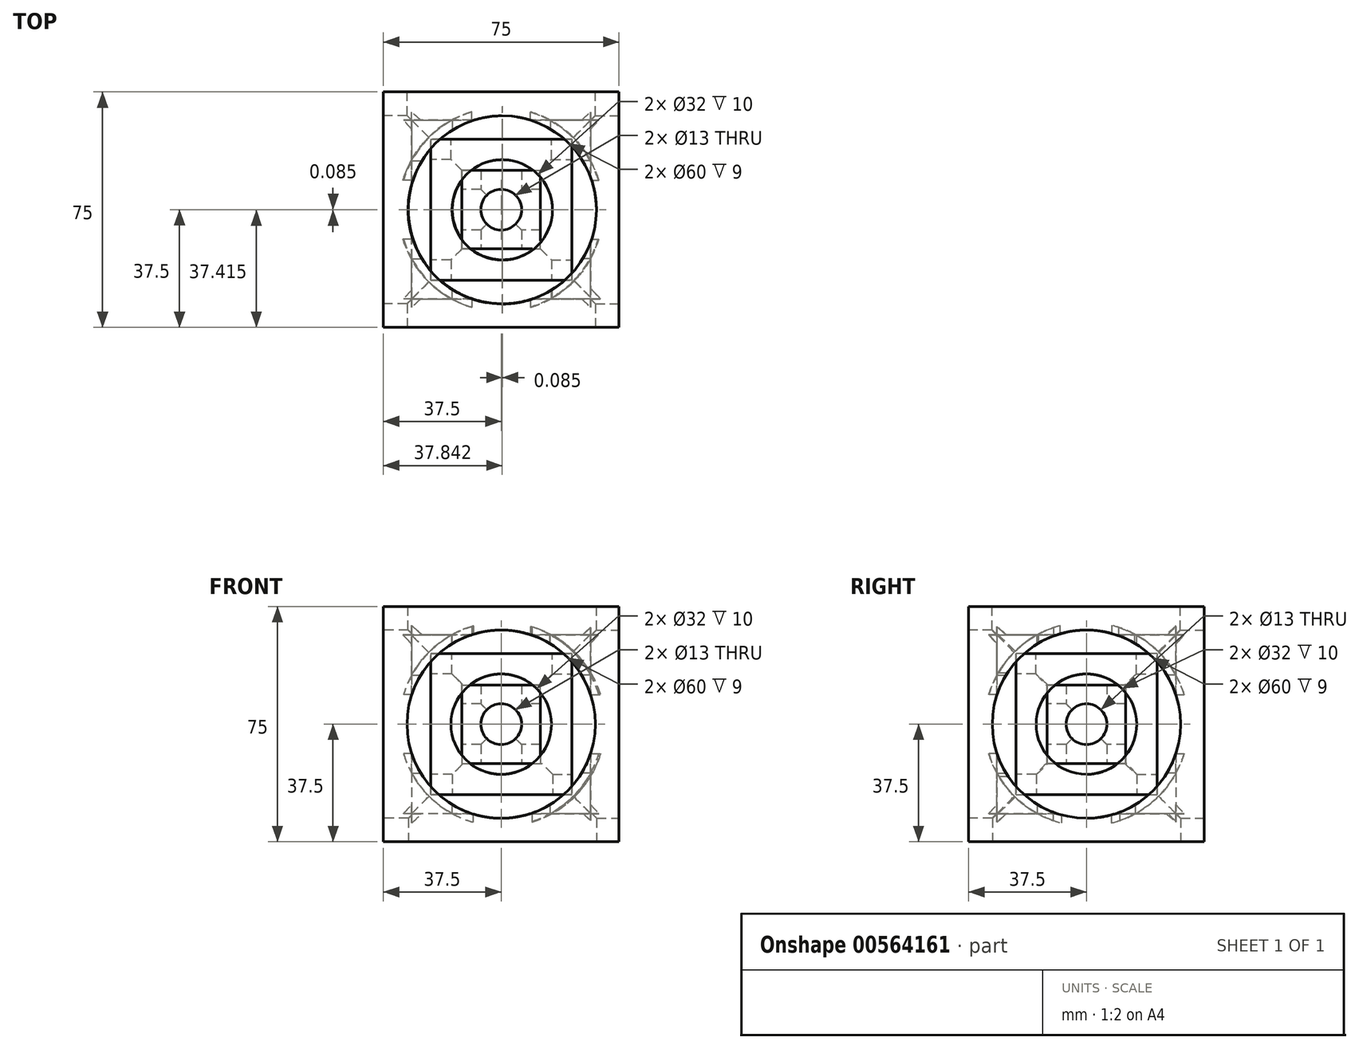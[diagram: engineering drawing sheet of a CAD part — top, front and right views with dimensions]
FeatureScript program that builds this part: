
annotation { "Feature Type Name" : "Feature", "Feature Type Description" : "" }
export const myFeature = defineFeature(function(context is Context, id is Id, definition is map)
    precondition{}
    {
        {
            assignVariable(context, id + "F0", {"name" : "S0", "anyValue" : 75});
        }
        {
            assignVariable(context, id + "F1", {"name" : "D1", "anyValue" : 15});
        }
        {
            assignVariable(context, id + "F2", {"name" : "D2", "anyValue" : 10});
        }
        {
            assignVariable(context, id + "F3", {"name" : "UcutW", "anyValue" : 6});
        }
        {
            var Q0;
            Q0=qCreatedBy(makeId("Front.planeOp"),FACE);
            var sketch = newSketch(context, id + "F4", { "sketchPlane" : qUnion([Q0])});
            skLineSegment(sketch, "E0", {"start": v(0, 0) * mm, "end": v(37.5, 0) * mm, "construction": true});
            skLineSegment(sketch, "E1", {"start": v(37.5, 0) * mm, "end": v(37.5, 37.5) * mm});
            skLineSegment(sketch, "E2", {"start": v(37.5, 37.5) * mm, "end": v(-37.5, 37.5) * mm});
            skLineSegment(sketch, "E3", {"start": v(-37.5, 37.5) * mm, "end": v(-37.5, -37.5) * mm});
            skLineSegment(sketch, "E4", {"start": v(-37.5, -37.5) * mm, "end": v(37.5, -37.5) * mm});
            skLineSegment(sketch, "E5", {"start": v(37.5, -37.5) * mm, "end": v(37.5, 0) * mm});
            skSolve(sketch);
        }
        {
            var Q0;
            Q0 = qSketchRegion(id + "F4", true);
            extrude(context, id + "F5", {"entities" : qUnion([Q0]), "depth" : (getVariable(context, 'S0')) * mm, "offsetDistance" : 25 * mm, "symmetric" : true});
        }
        {
            var Q0;
            Q0=makeQuery(id+"F5.opExtrude","CAP_FACE",FACE,{"disambiguationData":[OSD([sQuery(id+"F4.wireOp",EDGE,"E1"),sQuery(id+"F4.wireOp",EDGE,"E2"),sQuery(id+"F4.wireOp",EDGE,"E3"),sQuery(id+"F4.wireOp",EDGE,"E4"),sQuery(id+"F4.wireOp",EDGE,"E5")])],"isStart":true});
            var sketch = newSketch(context, id + "F6", { "sketchPlane" : qUnion([Q0])});
            skCircle(sketch, "E6", {"center": v(0, 0) * mm, "radius": 30 * mm});
            skCircle(sketch, "E7", {"center": v(0, 0) * mm, "radius": 16 * mm});
            skText(sketch, "E8", { "text": "Ref face", "fontName": "OpenSans-Regular.ttf"});
            const initialGuessF6  = {"E8": [0.0082, -0.03528, 1, 0, 0.0053]};
            skSetInitialGuess(sketch, initialGuessF6);
            skSolve(sketch);
        }
        {
            var Q0;
            Q0=makeQuery(id+"F6.imprint","IMPRINT",FACE,{"disambiguationData":[TD([[makeQuery(id+"F6.imprint","IMPRINT",EDGE,{"derivedFrom":sQuery(id+"F6.wireOp",EDGE,"E6")}),1.0]])]});
            extrude(context, id + "F7", {"entities" : qUnion([Q0]), "operationType" : NewBodyOperationType.REMOVE, "oppositeDirection" : true, "depth" : (getVariable(context, 'D1')) * mm, "offsetDistance" : 25 * mm});
        }
        {
            var Q0;
            Q0=makeQuery(id+"F7.boolean.opBoolean","SPLIT",FACE,{"disambiguationData":[TD([makeQuery(id+"F7.opExtrude","SWEPT_FACE",FACE,{"disambiguationData":[OSD([sQuery(id+"F6.wireOp",EDGE,"E7")])]})])],"derivedFrom":makeQuery(id+"F5.opExtrude","CAP_FACE",FACE,{"disambiguationData":[OSD([sQuery(id+"F4.wireOp",EDGE,"E1"),sQuery(id+"F4.wireOp",EDGE,"E2"),sQuery(id+"F4.wireOp",EDGE,"E3"),sQuery(id+"F4.wireOp",EDGE,"E4"),sQuery(id+"F4.wireOp",EDGE,"E5")])],"isStart":true})});
            extrude(context, id + "F8", {"entities" : qUnion([Q0]), "operationType" : NewBodyOperationType.REMOVE, "oppositeDirection" : true, "depth" : (getVariable(context, 'D1') + getVariable(context, 'D2')) * mm, "offsetDistance" : 25 * mm});
        }
        {
            var Q0;
            Q0=makeQuery(id+"F5.opExtrude","SWEPT_FACE",FACE,{"disambiguationData":[OSD([sQuery(id+"F4.wireOp",EDGE,"E3")])]});
            var sketch = newSketch(context, id + "F9", { "sketchPlane" : qUnion([Q0])});
            skCircle(sketch, "E9", {"center": v(0, 0) * mm, "radius": 30 * mm});
            skCircle(sketch, "E10", {"center": v(0, 0) * mm, "radius": 16 * mm});
            skSolve(sketch);
        }
        {
            var Q0;
            Q0=makeQuery(id+"F9.imprint","IMPRINT",FACE,{"disambiguationData":[TD([[makeQuery(id+"F9.imprint","IMPRINT",EDGE,{"derivedFrom":sQuery(id+"F9.wireOp",EDGE,"E9")}),1.0]])]});
            extrude(context, id + "F10", {"entities" : qUnion([Q0]), "operationType" : NewBodyOperationType.REMOVE, "oppositeDirection" : true, "depth" : (getVariable(context, 'D1')) * mm, "offsetDistance" : 25 * mm});
        }
        {
            var Q0;
            Q0=makeQuery(id+"F10.boolean.opBoolean","SPLIT",FACE,{"disambiguationData":[TD([makeQuery(id+"F10.opExtrude","SWEPT_FACE",FACE,{"disambiguationData":[OSD([sQuery(id+"F9.wireOp",EDGE,"E10")])]})])],"derivedFrom":makeQuery(id+"F5.opExtrude","SWEPT_FACE",FACE,{"disambiguationData":[OSD([sQuery(id+"F4.wireOp",EDGE,"E3")])]})});
            extrude(context, id + "F11", {"entities" : qUnion([Q0]), "operationType" : NewBodyOperationType.REMOVE, "oppositeDirection" : true, "depth" : (getVariable(context, 'D1') + getVariable(context, 'D2')) * mm, "offsetDistance" : 25 * mm});
        }
        {
            var Q0;
            Q0=makeQuery(id+"F5.opExtrude","CAP_FACE",FACE,{"disambiguationData":[OSD([sQuery(id+"F4.wireOp",EDGE,"E1"),sQuery(id+"F4.wireOp",EDGE,"E2"),sQuery(id+"F4.wireOp",EDGE,"E3"),sQuery(id+"F4.wireOp",EDGE,"E4"),sQuery(id+"F4.wireOp",EDGE,"E5")])],"isStart":false});
            var sketch = newSketch(context, id + "F12", { "sketchPlane" : qUnion([Q0])});
            skCircle(sketch, "E11", {"center": v(0, 0) * mm, "radius": 30 * mm});
            skCircle(sketch, "E12", {"center": v(0, 0) * mm, "radius": 16 * mm});
            skSolve(sketch);
        }
        {
            var Q0;
            Q0=makeQuery(id+"F12.imprint","IMPRINT",FACE,{"disambiguationData":[TD([[makeQuery(id+"F12.imprint","IMPRINT",EDGE,{"derivedFrom":sQuery(id+"F12.wireOp",EDGE,"E11")}),1.0]])]});
            extrude(context, id + "F13", {"entities" : qUnion([Q0]), "operationType" : NewBodyOperationType.REMOVE, "oppositeDirection" : true, "depth" : (getVariable(context, 'D1')) * mm, "offsetDistance" : 25 * mm});
        }
        {
            var Q0;
            Q0=makeQuery(id+"F13.boolean.opBoolean","SPLIT",FACE,{"disambiguationData":[TD([makeQuery(id+"F13.opExtrude","SWEPT_FACE",FACE,{"disambiguationData":[OSD([sQuery(id+"F12.wireOp",EDGE,"E12")])]})])],"derivedFrom":makeQuery(id+"F5.opExtrude","CAP_FACE",FACE,{"disambiguationData":[OSD([sQuery(id+"F4.wireOp",EDGE,"E1"),sQuery(id+"F4.wireOp",EDGE,"E2"),sQuery(id+"F4.wireOp",EDGE,"E3"),sQuery(id+"F4.wireOp",EDGE,"E4"),sQuery(id+"F4.wireOp",EDGE,"E5")])],"isStart":false})});
            extrude(context, id + "F14", {"entities" : qUnion([Q0]), "operationType" : NewBodyOperationType.REMOVE, "oppositeDirection" : true, "depth" : (getVariable(context, 'D1') + getVariable(context, 'D2')) * mm, "offsetDistance" : 25 * mm});
        }
        {
            var Q0;
            Q0=makeQuery(id+"F5.opExtrude","SWEPT_FACE",FACE,{"disambiguationData":[OSD([sQuery(id+"F4.wireOp",EDGE,"E1"),sQuery(id+"F4.wireOp",EDGE,"E5")])]});
            var sketch = newSketch(context, id + "F15", { "sketchPlane" : qUnion([Q0])});
            skCircle(sketch, "E13", {"center": v(0, 0) * mm, "radius": 30 * mm});
            skCircle(sketch, "E14", {"center": v(0, 0) * mm, "radius": 16 * mm});
            skSolve(sketch);
        }
        {
            var Q0;
            Q0=makeQuery(id+"F15.imprint","IMPRINT",FACE,{"disambiguationData":[TD([[makeQuery(id+"F15.imprint","IMPRINT",EDGE,{"derivedFrom":sQuery(id+"F15.wireOp",EDGE,"E13")}),1.0]])]});
            extrude(context, id + "F16", {"entities" : qUnion([Q0]), "operationType" : NewBodyOperationType.REMOVE, "oppositeDirection" : true, "depth" : (getVariable(context, 'D1')) * mm, "offsetDistance" : 25 * mm});
        }
        {
            var Q0;
            Q0=makeQuery(id+"F16.boolean.opBoolean","SPLIT",FACE,{"disambiguationData":[TD([makeQuery(id+"F16.opExtrude","SWEPT_FACE",FACE,{"disambiguationData":[OSD([sQuery(id+"F15.wireOp",EDGE,"E14")])]})])],"derivedFrom":makeQuery(id+"F5.opExtrude","SWEPT_FACE",FACE,{"disambiguationData":[OSD([sQuery(id+"F4.wireOp",EDGE,"E1"),sQuery(id+"F4.wireOp",EDGE,"E5")])]})});
            extrude(context, id + "F17", {"entities" : qUnion([Q0]), "operationType" : NewBodyOperationType.REMOVE, "oppositeDirection" : true, "depth" : (getVariable(context, 'D1') + getVariable(context, 'D2')) * mm, "offsetDistance" : 25 * mm});
        }
        {
            var Q0;
            Q0=makeQuery(id+"F5.opExtrude","SWEPT_FACE",FACE,{"disambiguationData":[OSD([sQuery(id+"F4.wireOp",EDGE,"E2")])]});
            var sketch = newSketch(context, id + "F18", { "sketchPlane" : qUnion([Q0])});
            skCircle(sketch, "E15", {"center": v(0.34, -0.09) * mm, "radius": 30 * mm});
            skCircle(sketch, "E16", {"center": v(0.34, -0.09) * mm, "radius": 16 * mm});
            skSolve(sketch);
        }
        {
            var Q0;
            Q0=makeQuery(id+"F18.imprint","IMPRINT",FACE,{"disambiguationData":[TD([[makeQuery(id+"F18.imprint","IMPRINT",EDGE,{"derivedFrom":sQuery(id+"F18.wireOp",EDGE,"E15")}),1.0]])]});
            extrude(context, id + "F19", {"entities" : qUnion([Q0]), "operationType" : NewBodyOperationType.REMOVE, "oppositeDirection" : true, "depth" : (getVariable(context, 'D1')) * mm, "offsetDistance" : 25 * mm});
        }
        {
            var Q0;
            Q0=makeQuery(id+"F19.boolean.opBoolean","SPLIT",FACE,{"disambiguationData":[TD([makeQuery(id+"F19.opExtrude","SWEPT_FACE",FACE,{"disambiguationData":[OSD([sQuery(id+"F18.wireOp",EDGE,"E16")])]})])],"derivedFrom":makeQuery(id+"F5.opExtrude","SWEPT_FACE",FACE,{"disambiguationData":[OSD([sQuery(id+"F4.wireOp",EDGE,"E2")])]})});
            extrude(context, id + "F20", {"entities" : qUnion([Q0]), "operationType" : NewBodyOperationType.REMOVE, "oppositeDirection" : true, "depth" : (getVariable(context, 'D1') + getVariable(context, 'D2')) * mm, "offsetDistance" : 25 * mm});
        }
        {
            var Q0;
            Q0=makeQuery(id+"F5.opExtrude","SWEPT_FACE",FACE,{"disambiguationData":[OSD([sQuery(id+"F4.wireOp",EDGE,"E4")])]});
            var sketch = newSketch(context, id + "F21", { "sketchPlane" : qUnion([Q0])});
            skCircle(sketch, "E17", {"center": v(0.43, 0) * mm, "radius": 30 * mm});
            skCircle(sketch, "E18", {"center": v(0.43, 0) * mm, "radius": 16 * mm});
            skSolve(sketch);
        }
        {
            var Q0;
            Q0=makeQuery(id+"F21.imprint","IMPRINT",FACE,{"disambiguationData":[TD([[makeQuery(id+"F21.imprint","IMPRINT",EDGE,{"derivedFrom":sQuery(id+"F21.wireOp",EDGE,"E17")}),1.0]])]});
            extrude(context, id + "F22", {"entities" : qUnion([Q0]), "operationType" : NewBodyOperationType.REMOVE, "oppositeDirection" : true, "depth" : (getVariable(context, 'D1')) * mm, "offsetDistance" : 25 * mm});
        }
        {
            var Q0;
            Q0=makeQuery(id+"F22.boolean.opBoolean","SPLIT",FACE,{"disambiguationData":[TD([makeQuery(id+"F22.opExtrude","SWEPT_FACE",FACE,{"disambiguationData":[OSD([sQuery(id+"F21.wireOp",EDGE,"E18")])]})])],"derivedFrom":makeQuery(id+"F5.opExtrude","SWEPT_FACE",FACE,{"disambiguationData":[OSD([sQuery(id+"F4.wireOp",EDGE,"E4")])]})});
            extrude(context, id + "F23", {"entities" : qUnion([Q0]), "operationType" : NewBodyOperationType.REMOVE, "oppositeDirection" : true, "depth" : (getVariable(context, 'D1') + getVariable(context, 'D2')) * mm, "offsetDistance" : 25 * mm});
        }
        {
            var Q0;
            Q0=makeQuery(id+"F11.boolean.opBoolean","COPY",FACE,{"derivedFrom":makeQuery(id+"F11.opExtrude","CAP_FACE",FACE,{"disambiguationData":[OSD([sQuery(id+"F4.wireOp",EDGE,"E3")])],"isStart":false})});
            var sketch = newSketch(context, id + "F24", { "sketchPlane" : qUnion([Q0])});
            skCircle(sketch, "E19", {"center": v(0, 0) * mm, "radius": 6.5 * mm});
            skSolve(sketch);
        }
        {
            var Q0;
            Q0 = qSketchRegion(id + "F24", true);
            extrude(context, id + "F25", {"entities" : qUnion([Q0]), "operationType" : NewBodyOperationType.REMOVE, "endBound" : BoundingType.THROUGH_ALL, "oppositeDirection" : true, "depth" : 25 * mm, "offsetDistance" : 25 * mm});
        }
        {
            var Q0;
            Q0=makeQuery(id+"F14.boolean.opBoolean","COPY",FACE,{"derivedFrom":makeQuery(id+"F14.opExtrude","CAP_FACE",FACE,{"disambiguationData":[OSD([sQuery(id+"F4.wireOp",EDGE,"E1"),sQuery(id+"F4.wireOp",EDGE,"E2"),sQuery(id+"F4.wireOp",EDGE,"E3"),sQuery(id+"F4.wireOp",EDGE,"E4"),sQuery(id+"F4.wireOp",EDGE,"E5")])],"isStart":false})});
            var sketch = newSketch(context, id + "F26", { "sketchPlane" : qUnion([Q0])});
            skCircle(sketch, "E20", {"center": v(0, 0) * mm, "radius": 6.5 * mm});
            skSolve(sketch);
        }
        {
            var Q0;
            Q0 = qSketchRegion(id + "F26", true);
            extrude(context, id + "F27", {"entities" : qUnion([Q0]), "operationType" : NewBodyOperationType.REMOVE, "endBound" : BoundingType.THROUGH_ALL, "oppositeDirection" : true, "depth" : 25 * mm, "offsetDistance" : 25 * mm});
        }
        {
            var Q0;
            Q0=makeQuery(id+"F23.boolean.opBoolean","COPY",FACE,{"derivedFrom":makeQuery(id+"F23.opExtrude","CAP_FACE",FACE,{"disambiguationData":[OSD([sQuery(id+"F4.wireOp",EDGE,"E4")])],"isStart":false})});
            var sketch = newSketch(context, id + "F28", { "sketchPlane" : qUnion([Q0])});
            skCircle(sketch, "E21", {"center": v(0, 0) * mm, "radius": 6.5 * mm});
            skSolve(sketch);
        }
        {
            var Q0;
            Q0 = qSketchRegion(id + "F28", true);
            extrude(context, id + "F29", {"entities" : qUnion([Q0]), "operationType" : NewBodyOperationType.REMOVE, "endBound" : BoundingType.THROUGH_ALL, "oppositeDirection" : true, "depth" : 25 * mm, "offsetDistance" : 25 * mm});
        }
        {
            var Q0;
            Q0=makeQuery(id+"F13.boolean.opBoolean","COPY",FACE,{"derivedFrom":makeQuery(id+"F13.opExtrude","CAP_FACE",FACE,{"disambiguationData":[OSD([sQuery(id+"F12.wireOp",EDGE,"E11"),sQuery(id+"F12.wireOp",EDGE,"E12")])],"isStart":false})});
            var sketch = newSketch(context, id + "F30", { "sketchPlane" : qUnion([Q0])});
            skCircle(sketch, "E22", {"center": v(0, 0) * mm, "radius": 32.5 * mm});
            skSolve(sketch);
        }
        {
            var Q0;
            Q0=makeQuery(id+"F30.imprint","IMPRINT",FACE,{"disambiguationData":[TD([[makeQuery(id+"F30.imprint","IMPRINT",EDGE,{"derivedFrom":sQuery(id+"F30.wireOp",EDGE,"E22")}),1.0]])]});
            extrude(context, id + "F31", {"entities" : qUnion([Q0]), "operationType" : NewBodyOperationType.REMOVE, "depth" : (getVariable(context, 'UcutW')) * mm, "offsetDistance" : 25 * mm});
        }
        {
            var Q0;
            Q0=makeQuery(id+"F16.boolean.opBoolean","COPY",FACE,{"derivedFrom":makeQuery(id+"F16.opExtrude","CAP_FACE",FACE,{"disambiguationData":[OSD([sQuery(id+"F15.wireOp",EDGE,"E13"),sQuery(id+"F15.wireOp",EDGE,"E14")])],"isStart":false})});
            var sketch = newSketch(context, id + "F32", { "sketchPlane" : qUnion([Q0])});
            skCircle(sketch, "E23", {"center": v(0, 0) * mm, "radius": 32.5 * mm});
            skSolve(sketch);
        }
        {
            var Q0;
            Q0 = qSketchRegion(id + "F32", true);
            extrude(context, id + "F33", {"entities" : qUnion([Q0]), "operationType" : NewBodyOperationType.REMOVE, "depth" : (getVariable(context, 'UcutW')) * mm, "offsetDistance" : 25 * mm});
        }
        {
            var Q0;
            Q0=makeQuery(id+"F19.boolean.opBoolean","COPY",FACE,{"derivedFrom":makeQuery(id+"F19.opExtrude","CAP_FACE",FACE,{"disambiguationData":[OSD([sQuery(id+"F18.wireOp",EDGE,"E15"),sQuery(id+"F18.wireOp",EDGE,"E16")])],"isStart":false})});
            var sketch = newSketch(context, id + "F34", { "sketchPlane" : qUnion([Q0])});
            skCircle(sketch, "E24", {"center": v(-0.17, 0.02) * mm, "radius": 32.5 * mm});
            skSolve(sketch);
        }
        {
            var Q0;
            Q0 = qSketchRegion(id + "F34", true);
            var Q1;
            Q1 = qConstructionFilter(qBodyType(qCreatedBy(id + "F34" ,EDGE), BodyType.WIRE), ConstructionObject.NO);
            extrude(context, id + "F35", {"entities" : qUnion([Q0]), "operationType" : NewBodyOperationType.REMOVE, "surfaceEntities" : qUnion([Q1]), "depth" : (getVariable(context, 'UcutW')) * mm, "offsetDistance" : 25 * mm});
        }
        {
            var Q0;
            {var subQ0=sQuery(id+"F21.wireOp",EDGE,"E17");var subQ1=makeQuery(id+"F22.boolean.opBoolean","COPY",FACE,{"derivedFrom":makeQuery(id+"F22.opExtrude","SWEPT_FACE",FACE,{"disambiguationData":[OSD([subQ0])]})});var subQ2=sQuery(id+"F30.wireOp",EDGE,"E22");var subQ3=makeQuery(id+"F31.opExtrude","CAP_FACE",FACE,{"disambiguationData":[OSD([subQ2])],"isStart":true});var subQ4=sQuery(id+"F9.wireOp",EDGE,"E9");var subQ5=makeQuery(id+"F10.boolean.opBoolean","COPY",FACE,{"derivedFrom":makeQuery(id+"F10.opExtrude","SWEPT_FACE",FACE,{"disambiguationData":[OSD([subQ4])]})});var subQ6=sQuery(id+"F12.wireOp",EDGE,"E12");var subQ7=sQuery(id+"F12.wireOp",EDGE,"E11");var subQ8=makeQuery(id+"F13.boolean.opBoolean","COPY",FACE,{"derivedFrom":makeQuery(id+"F13.opExtrude","CAP_FACE",FACE,{"disambiguationData":[OSD([subQ7,subQ6])],"isStart":false})});var subQ9=makeQuery(id+"F31.opExtrude","CAP_FACE",FACE,{"disambiguationData":[OSD([subQ2])],"isStart":false});var subQ10=makeQuery(id+"F31.opExtrude","SWEPT_FACE",FACE,{"disambiguationData":[OSD([subQ2])]});var subQ11=makeQuery(id+"F31.boolean.opBoolean","COPY",FACE,{"disambiguationData":[TD([subQ5,subQ8,subQ1,subQ3,subQ9])],"derivedFrom":subQ10});var subQ12=sQuery(id+"F18.wireOp",EDGE,"E15");var subQ13=makeQuery(id+"F19.boolean.opBoolean","COPY",FACE,{"derivedFrom":makeQuery(id+"F19.opExtrude","SWEPT_FACE",FACE,{"disambiguationData":[OSD([subQ12])]})});var subQ14=makeQuery(id+"F31.boolean.opBoolean","COPY",FACE,{"disambiguationData":[TD([subQ5,subQ8,subQ13,subQ3,subQ9])],"derivedFrom":subQ10});var subQ15=makeQuery(id+"F22.boolean.opBoolean","COPY",FACE,{"derivedFrom":makeQuery(id+"F22.opExtrude","CAP_FACE",FACE,{"disambiguationData":[OSD([subQ0,sQuery(id+"F21.wireOp",EDGE,"E18")])],"isStart":false})});var subQ16=makeQuery(id+"F19.boolean.opBoolean","COPY",FACE,{"derivedFrom":makeQuery(id+"F19.opExtrude","CAP_FACE",FACE,{"disambiguationData":[OSD([subQ12,sQuery(id+"F18.wireOp",EDGE,"E16")])],"isStart":false})});var subQ17=sQuery(id+"F15.wireOp",EDGE,"E13");var subQ18=makeQuery(id+"F16.boolean.opBoolean","COPY",FACE,{"derivedFrom":makeQuery(id+"F16.opExtrude","SWEPT_FACE",FACE,{"disambiguationData":[OSD([subQ17])]})});var subQ19=makeQuery(id+"F31.boolean.opBoolean","COPY",FACE,{"disambiguationData":[TD([subQ8,subQ18,subQ1,subQ3,subQ9])],"derivedFrom":subQ10});var subQ20=makeQuery(id+"F16.boolean.opBoolean","COPY",FACE,{"derivedFrom":makeQuery(id+"F16.opExtrude","CAP_FACE",FACE,{"disambiguationData":[OSD([subQ17,sQuery(id+"F15.wireOp",EDGE,"E14")])],"isStart":false})});var subQ21=sQuery(id+"F32.wireOp",EDGE,"E23");var subQ22=makeQuery(id+"F33.opExtrude","CAP_FACE",FACE,{"disambiguationData":[OSD([subQ21])],"isStart":true});var subQ23=makeQuery(id+"F33.opExtrude","SWEPT_FACE",FACE,{"disambiguationData":[OSD([subQ21])]});var subQ24=makeQuery(id+"F10.boolean.opBoolean","COPY",FACE,{"derivedFrom":makeQuery(id+"F10.opExtrude","CAP_FACE",FACE,{"disambiguationData":[OSD([subQ4,sQuery(id+"F9.wireOp",EDGE,"E10")])],"isStart":false})});var subQ25=makeQuery(id+"F14.boolean.opBoolean","COPY",FACE,{"derivedFrom":makeQuery(id+"F14.opExtrude","SWEPT_FACE",FACE,{"disambiguationData":[OSD([subQ6])]})});Q0=makeQuery(id+"F35.boolean.opBoolean","SPLIT",FACE,{"disambiguationData":[TD([subQ5,subQ24,subQ25,subQ20,subQ16,subQ1,subQ15,subQ14,subQ11,subQ19,subQ22,makeQuery(id+"F33.boolean.opBoolean","COPY",FACE,{"disambiguationData":[TD([subQ8,subQ20,subQ1,subQ3,subQ19,makeQuery(id+"F31.boolean.opBoolean","COPY",FACE,{"disambiguationData":[TD([makeQuery(id+"F13.boolean.opBoolean","COPY",FACE,{"derivedFrom":makeQuery(id+"F13.opExtrude","SWEPT_FACE",FACE,{"disambiguationData":[OSD([subQ7])]})}),subQ18,subQ1,subQ10])],"derivedFrom":subQ9}),subQ23,subQ22,makeQuery(id+"F33.opExtrude","CAP_FACE",FACE,{"disambiguationData":[OSD([subQ21])],"isStart":false})])],"derivedFrom":subQ23}),makeQuery(id+"F35.opExtrude","CAP_FACE",FACE,{"disambiguationData":[OSD([sQuery(id+"F34.wireOp",EDGE,"E24")])],"isStart":true})])],"derivedFrom":makeQuery(id+"F33.boolean.opBoolean","SPLIT",FACE,{"disambiguationData":[TD([subQ5,subQ24,subQ25,subQ20,subQ13,subQ16,subQ1,subQ15,subQ14,makeQuery(id+"F31.boolean.opBoolean","COPY",FACE,{"disambiguationData":[TD([subQ8,subQ18,subQ13,subQ3,subQ9])],"derivedFrom":subQ10}),subQ11,subQ19,subQ23,subQ22])],"derivedFrom":makeQuery(id+"F31.boolean.opBoolean","MERGE",FACE,{"derivedFrom":[subQ8,subQ3]})})});}
            var sketch = newSketch(context, id + "F36", { "sketchPlane" : qUnion([Q0])});
            skCircle(sketch, "E25", {"center": v(0.5, -0.06) * mm, "radius": 32.5 * mm});
            skSolve(sketch);
        }
        {
            var Q0;
            Q0 = qSketchRegion(id + "F36", true);
            extrude(context, id + "F37", {"entities" : qUnion([Q0]), "operationType" : NewBodyOperationType.REMOVE, "depth" : (getVariable(context, 'UcutW')) * mm, "offsetDistance" : 25 * mm});
        }
        {
            var Q0;
            Q0=makeQuery(id+"F22.boolean.opBoolean","COPY",FACE,{"derivedFrom":makeQuery(id+"F22.opExtrude","CAP_FACE",FACE,{"disambiguationData":[OSD([sQuery(id+"F21.wireOp",EDGE,"E17"),sQuery(id+"F21.wireOp",EDGE,"E18")])],"isStart":false})});
            var sketch = newSketch(context, id + "F38", { "sketchPlane" : qUnion([Q0])});
            skCircle(sketch, "E26", {"center": v(0, 0) * mm, "radius": 32.5 * mm});
            skSolve(sketch);
        }
        {
            var Q0;
            Q0 = qSketchRegion(id + "F38", true);
            extrude(context, id + "F39", {"entities" : qUnion([Q0]), "operationType" : NewBodyOperationType.REMOVE, "depth" : (getVariable(context, 'UcutW')) * mm, "offsetDistance" : 25 * mm});
        }
        {
            var Q0;
            Q0=makeQuery(id+"F7.boolean.opBoolean","COPY",FACE,{"derivedFrom":makeQuery(id+"F7.opExtrude","CAP_FACE",FACE,{"disambiguationData":[OSD([sQuery(id+"F6.wireOp",EDGE,"E6"),sQuery(id+"F6.wireOp",EDGE,"E7")])],"isStart":false})});
            var sketch = newSketch(context, id + "F40", { "sketchPlane" : qUnion([Q0])});
            skCircle(sketch, "E27", {"center": v(0, 0) * mm, "radius": 32.5 * mm});
            skSolve(sketch);
        }
        {
            var Q0;
            Q0 = qSketchRegion(id + "F40", true);
            var Q1;
            Q1 = qConstructionFilter(qBodyType(qCreatedBy(id + "F40" ,EDGE), BodyType.WIRE), ConstructionObject.NO);
            extrude(context, id + "F41", {"entities" : qUnion([Q0]), "operationType" : NewBodyOperationType.REMOVE, "surfaceEntities" : qUnion([Q1]), "depth" : (getVariable(context, 'UcutW')) * mm, "offsetDistance" : 25 * mm});
        }
        {
            var Q0;
            Q0=makeQuery(id+"F10.boolean.opBoolean","COPY",FACE,{"derivedFrom":makeQuery(id+"F10.opExtrude","CAP_FACE",FACE,{"disambiguationData":[OSD([sQuery(id+"F9.wireOp",EDGE,"E9"),sQuery(id+"F9.wireOp",EDGE,"E10")])],"isStart":false})});
            var sketch = newSketch(context, id + "F42", { "sketchPlane" : qUnion([Q0])});
            skCircle(sketch, "E28", {"center": v(0, 0) * mm, "radius": 32.5 * mm});
            skSolve(sketch);
        }
        {
            var Q0;
            Q0=makeQuery(id+"F42.imprint","IMPRINT",FACE,{"disambiguationData":[TD([[makeQuery(id+"F42.imprint","IMPRINT",EDGE,{"derivedFrom":sQuery(id+"F42.wireOp",EDGE,"E28")}),1.0]])]});
            extrude(context, id + "F43", {"entities" : qUnion([Q0]), "operationType" : NewBodyOperationType.REMOVE, "depth" : (getVariable(context, 'UcutW')) * mm, "offsetDistance" : 25 * mm});
        }
    });
